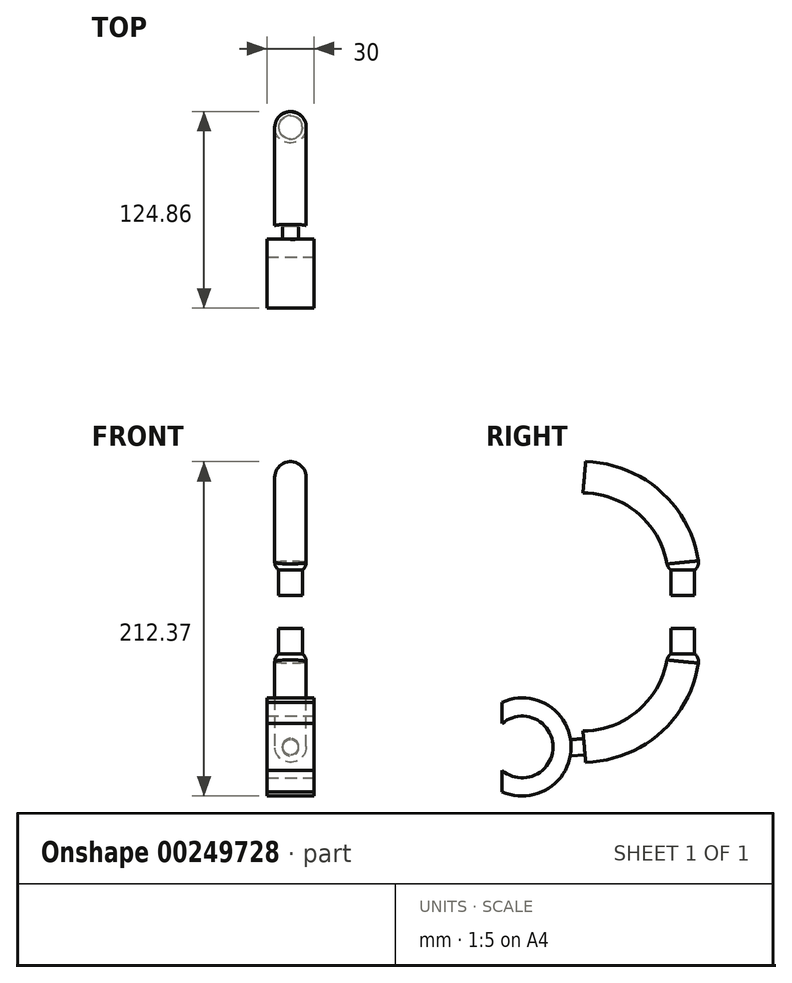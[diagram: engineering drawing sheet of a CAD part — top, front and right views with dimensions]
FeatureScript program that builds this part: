
annotation { "Feature Type Name" : "Feature", "Feature Type Description" : "" }
export const myFeature = defineFeature(function(context is Context, id is Id, definition is map)
    precondition{}
    {
        {
            var Q0;
            Q0=qCreatedBy(makeId("Top.planeOp"),FACE);
            var sketch = newSketch(context, id + "F0", { "sketchPlane" : qUnion([Q0])});
            skCircle(sketch, "E0", {"center": v(-10, 0) * mm, "radius": 10 * mm});
            skPoint(sketch, "E1", {"position": v(0, 0) * mm});
            skSolve(sketch);
        }
        {
            var Q0;
            Q0=qCreatedBy(makeId("Right.planeOp"),FACE);
            var sketch = newSketch(context, id + "F1", { "sketchPlane" : qUnion([Q0])});
            skArc(sketch, "E2", {"start": v(-63.22, -60) * mm, "mid": v(-19.94, -42.3) * mm, "end": v(0, 0) * mm});
            skSolve(sketch);
        }
        {
            var Q0;
            Q0=makeQuery(id+"F0.imprint","IMPRINT",FACE,{"disambiguationData":[TD([[makeQuery(id+"F0.imprint","IMPRINT",EDGE,{"derivedFrom":sQuery(id+"F0.wireOp",EDGE,"E0")}),1.0]])]});
            var Q1;
            Q1=sQuery(id+"F1.wireOp",EDGE,"E2");
            sweep(context, id + "F2", {"profiles" : qUnion([Q0]), "path" : qUnion([Q1])});
        }
        {
            var Q0;
            Q0=makeQuery(id+"F2.opSweep","CAP_EDGE",EDGE,{"disambiguationData":[OSD([sQuery(id+"F0.wireOp",EDGE,"E0"),sQuery(id+"F1.wireOp",VERTEX,"E2.end")])],"isStart":true});
            fillet(context, id + "F3", {"entities" : qUnion([Q0]), "radius" : 6 * mm, "tangentPropagation" : true, "allowEdgeOverflow" : false});
        }
        {
            var Q0;
            Q0=makeQuery(id+"F2.opSweep","CAP_FACE",FACE,{"disambiguationData":[OSD([sQuery(id+"F0.wireOp",EDGE,"E0"),sQuery(id+"F1.wireOp",VERTEX,"E2.end")])],"isStart":true});
            var sketch = newSketch(context, id + "F4", { "sketchPlane" : qUnion([Q0])});
            skFitSpline(sketch, "E3", {"points": [v(-20, -0.7) * mm, v(-20, -0.34) * mm, v(-19.96, 0.38) * mm, v(-19.8, 1.33) * mm, v(-19.6, 2.1) * mm, v(-19.41, 2.7) * mm, v(-19.17, 3.3) * mm, v(-18.88, 3.93) * mm, v(-18.52, 4.56) * mm, v(-18.1, 5.2) * mm, v(-17.66, 5.75) * mm, v(-17.26, 6.2) * mm, v(-16.93, 6.53) * mm, v(-16.56, 6.88) * mm, v(-16.14, 7.22) * mm, v(-15.75, 7.51) * mm, v(-15.4, 7.74) * mm, v(-15.11, 7.92) * mm, v(-14.8, 8.1) * mm, v(-14.46, 8.28) * mm, v(-14.09, 8.45) * mm, v(-13.73, 8.6) * mm, v(-13.42, 8.72) * mm, v(-13.16, 8.81) * mm, v(-12.88, 8.9) * mm, v(-12.61, 8.98) * mm, v(-12.38, 9.04) * mm, v(-12.19, 9.08) * mm, v(-11.98, 9.13) * mm, v(-11.75, 9.17) * mm, v(-11.52, 9.21) * mm, v(-11.32, 9.24) * mm, v(-11.15, 9.26) * mm, v(-10.96, 9.28) * mm, v(-10.76, 9.3) * mm, v(-10.58, 9.31) * mm, v(-10.42, 9.32) * mm, v(-10.23, 9.33) * mm, v(-10, 9.33) * mm, v(-9.77, 9.32) * mm, v(-9.58, 9.32) * mm, v(-9.42, 9.31) * mm, v(-9.23, 9.3) * mm, v(-9.04, 9.28) * mm, v(-8.85, 9.26) * mm, v(-8.68, 9.24) * mm, v(-8.48, 9.21) * mm, v(-8.25, 9.17) * mm, v(-8.02, 9.13) * mm, v(-7.81, 9.08) * mm, v(-7.62, 9.04) * mm, v(-7.39, 8.98) * mm, v(-7.12, 8.9) * mm, v(-6.84, 8.81) * mm, v(-6.58, 8.72) * mm, v(-6.27, 8.6) * mm, v(-5.91, 8.45) * mm, v(-5.54, 8.28) * mm, v(-5.2, 8.1) * mm, v(-4.89, 7.92) * mm, v(-4.6, 7.74) * mm, v(-4.25, 7.51) * mm, v(-3.86, 7.22) * mm, v(-3.44, 6.88) * mm, v(-3.07, 6.53) * mm, v(-2.74, 6.2) * mm, v(-2.34, 5.75) * mm, v(-1.9, 5.2) * mm, v(-1.48, 4.56) * mm, v(-1.12, 3.93) * mm, v(-0.83, 3.3) * mm, v(-0.59, 2.7) * mm, v(-0.4, 2.1) * mm, v(-0.2, 1.33) * mm, v(-0.04, 0.38) * mm, v(0, -0.34) * mm, v(0, -0.7) * mm], "construction": true});
            skLineSegment(sketch, "E4", {"start": v(0, -0.7) * mm, "end": v(-20, -0.7) * mm, "construction": true});
            skCircle(sketch, "E5", {"center": v(-10, -0.7) * mm, "radius": 7.5 * mm});
            skSolve(sketch);
        }
        {
            var Q0;
            {var subQ0=sQuery(id+"F1.wireOp",VERTEX,"E2.end");var subQ1=sQuery(id+"F0.wireOp",EDGE,"E0");Q0=makeQuery(id+"F4.imprint","IMPRINT",FACE,{"disambiguationData":[TD([[makeQuery(id+"F4.imprint","IMPRINT",EDGE,{"derivedFrom":makeQuery(id+"F3.opFillet","BLEND_EDGE",EDGE,{"blendedFrom":[makeQuery(id+"F2.opSweep","CAP_EDGE",EDGE,{"disambiguationData":[OSD([subQ1,subQ0])],"isStart":true}),makeQuery(id+"F2.opSweep","CAP_FACE",FACE,{"disambiguationData":[OSD([subQ1,subQ0])],"isStart":true})],"blendedInto":[makeQuery(id+"F2.opSweep","CAP_FACE",FACE,{"disambiguationData":[OSD([subQ1,subQ0])],"isStart":true})]})}),1.0]])]});}
            var Q1;
            Q1=makeQuery(id+"F4.imprint","IMPRINT",FACE,{"disambiguationData":[TD([[makeQuery(id+"F4.imprint","IMPRINT",EDGE,{"derivedFrom":sQuery(id+"F4.wireOp",EDGE,"E5")}),1.0]])]});
            extrude(context, id + "F5", {"entities" : qUnion([Q0, Q1]), "operationType" : NewBodyOperationType.ADD, "depth" : 15 * mm, "hasSecondDirection" : true, "secondDirectionOppositeDirection" : true, "secondDirectionDepth" : 5 * mm});
        }
        {
            var Q0;
            Q0=qCreatedBy(makeId("Front.planeOp"),FACE);
            var sketch = newSketch(context, id + "F6", { "sketchPlane" : qUnion([Q0])});
            skLineSegment(sketch, "E6", {"start": v(12.62, 25.53) * mm, "end": v(-28.31, 25.53) * mm});
            skSolve(sketch);
        }
        {
            var Q0;
            Q0=sQuery(id+"F6.wireOp",EDGE,"E6");
            cPlane(context, id + "F7", {"entities" : qUnion([Q0]), "cplaneType" : CPlaneType.LINE_ANGLE, "offset" : 25 * mm, "angle" : 90 * degree, "width" : 150 * mm, "height" : 150 * mm});
        }
        {
            var Q0;
            Q0=makeQuery(id+"F2.opSweep","CAP_FACE",FACE,{"disambiguationData":[OSD([sQuery(id+"F0.wireOp",EDGE,"E0"),sQuery(id+"F1.wireOp",VERTEX,"E2.start")])],"isStart":false});
            var sketch = newSketch(context, id + "F8", { "sketchPlane" : qUnion([Q0])});
            skCircle(sketch, "E7.0.0", {"center": v(-10, -54.26) * mm, "radius": 10 * mm, "construction": true});
            skLineSegment(sketch, "E8", {"start": v(-10, -38.42) * mm, "end": v(-10, -64.26) * mm, "construction": true});
            skSolve(sketch);
        }
        {
            var Q0;
            Q0=sQuery(id+"F8.wireOp",EDGE,"E8");
            cPlane(context, id + "F9", {"entities" : qUnion([Q0]), "cplaneType" : CPlaneType.LINE_ANGLE, "offset" : 25 * mm, "angle" : 0 * degree, "width" : 150 * mm, "height" : 150 * mm});
        }
        {
            var Q0;
            Q0=qCreatedBy(id+"F9.planeOp",FACE);
            var sketch = newSketch(context, id + "F10", { "sketchPlane" : qUnion([Q0])});
            skArc(sketch, "E9", {"start": v(102.72, -29.06) * mm, "mid": v(71.57, -60.21) * mm, "end": v(102.72, -91.36) * mm});
            skArc(sketch, "E10", {"start": v(102.72, -40.6) * mm, "mid": v(83.12, -60.21) * mm, "end": v(102.72, -79.82) * mm});
            skArc(sketch, "E11", {"start": v(115.53, -45.37) * mm, "mid": v(83.12, -60.21) * mm, "end": v(115.53, -75.05) * mm});
            skArc(sketch, "E12", {"start": v(115.53, -31.82) * mm, "mid": v(71.57, -60.21) * mm, "end": v(115.53, -88.6) * mm});
            skLineSegment(sketch, "E13", {"start": v(115.53, -31.82) * mm, "end": v(115.53, -45.37) * mm});
            skLineSegment(sketch, "E14.trimOffspring", {"start": v(115.53, -75.05) * mm, "end": v(115.53, -88.6) * mm});
            skSolve(sketch);
        }
        {
            var Q0;
            {var subQ0=sQuery(id+"F10.wireOp",EDGE,"E13");Q0=makeQuery(id+"F10.imprint","IMPRINT",FACE,{"disambiguationData":[TD([[makeQuery(id+"F10.imprint","IMPRINT",EDGE,{"derivedFrom":subQ0}),-1.0]])]});}
            extrude(context, id + "F11", {"entities" : qUnion([Q0]), "depth" : 15 * mm, "hasSecondDirection" : true, "secondDirectionOppositeDirection" : true, "secondDirectionDepth" : (15) * mm});
        }
        {
            var Q0;
            Q0=makeQuery(id+"F8.imprint","IMPRINT",FACE,{"disambiguationData":[TD([[makeQuery(id+"F8.imprint","IMPRINT",EDGE,{"derivedFrom":makeQuery(id+"F2.opSweep","CAP_EDGE",EDGE,{"disambiguationData":[OSD([sQuery(id+"F0.wireOp",EDGE,"E0"),sQuery(id+"F1.wireOp",VERTEX,"E2.start")])],"isStart":false})}),1.0]])]});
            var sketch = newSketch(context, id + "F12", { "sketchPlane" : qUnion([Q0])});
            skPoint(sketch, "E15.0", {"position": v(-10, -54.26) * mm});
            skCircle(sketch, "E16", {"center": v(-10, -54.26) * mm, "radius": 5.15 * mm});
            skSolve(sketch);
        }
        {
            var Q0;
            Q0 = qSketchRegion(id + "F12", true);
            extrude(context, id + "F13", {"entities" : qUnion([Q0]), "endBound" : BoundingType.UP_TO_NEXT, "depth" : 25 * mm});
        }
        {
            var Q0;
            Q0=makeQuery(id+"F2.opSweep","SWEPT_BODY",BODY,{"disambiguationData":[OSD([sQuery(id+"F0.wireOp",EDGE,"E0"),sQuery(id+"F1.wireOp",EDGE,"E2")])]});
            var Q1;
            Q1=qCreatedBy(id+"F7.planeOp",FACE);
            mirror(context, id + "F14", {"entities" : qUnion([Q0]), "mirrorPlane" : qUnion([Q1])});
        }
    });
